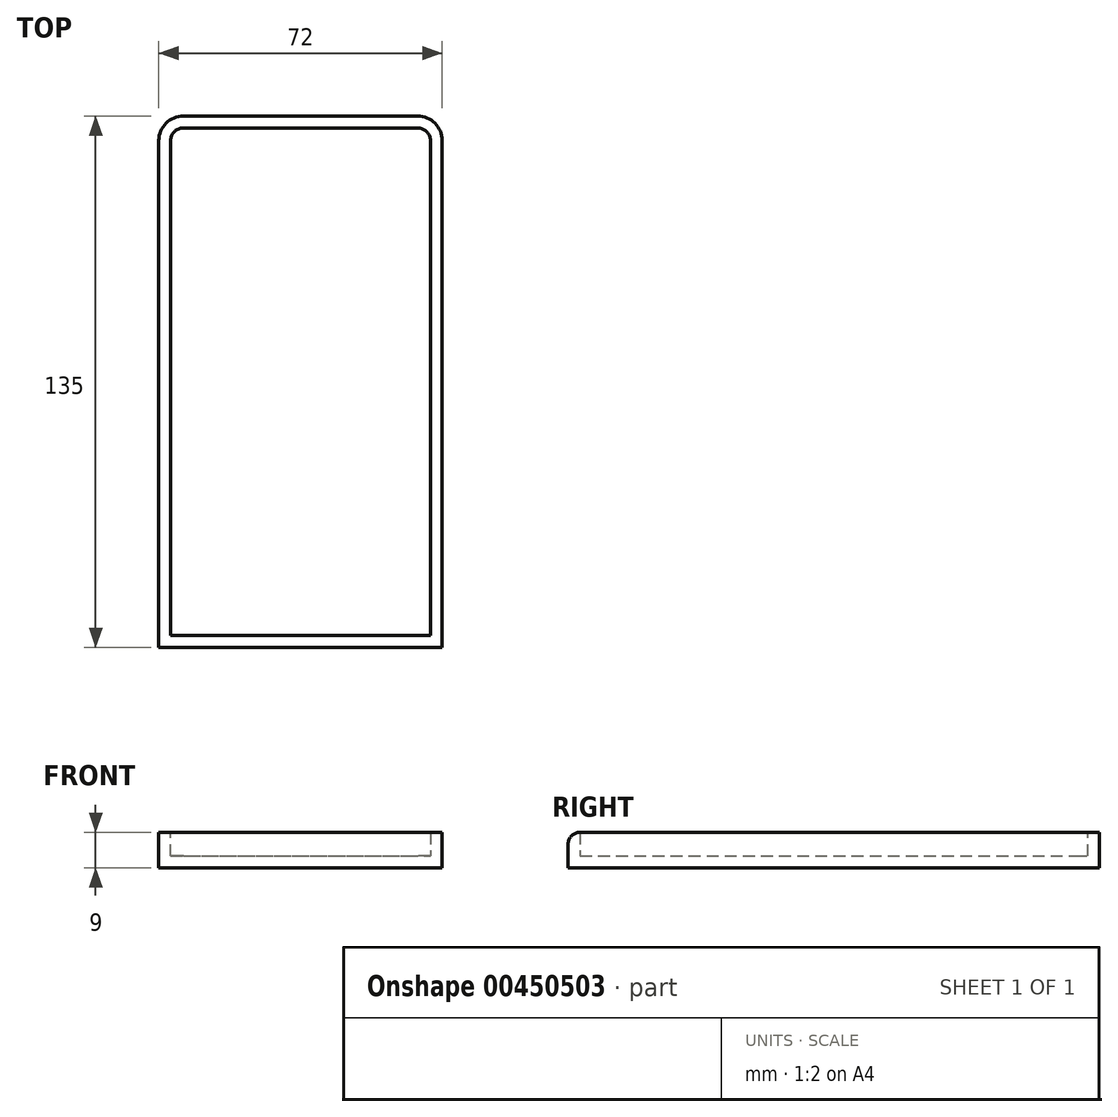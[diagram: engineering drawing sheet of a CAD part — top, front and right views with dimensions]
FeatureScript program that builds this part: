
annotation { "Feature Type Name" : "Feature", "Feature Type Description" : "" }
export const myFeature = defineFeature(function(context is Context, id is Id, definition is map)
    precondition{}
    {
        {
            var Q0;
            Q0=qCreatedBy(makeId("Top.planeOp"),FACE);
            var sketch = newSketch(context, id + "F0", { "sketchPlane" : qUnion([Q0])});
            skLineSegment(sketch, "E0.bottom", {"start": v(-74.36, -53.55) * mm, "end": v(-2.36, -53.55) * mm});
            skLineSegment(sketch, "E0.top", {"start": v(-68.1, 81.45) * mm, "end": v(-8.6, 81.45) * mm});
            skLineSegment(sketch, "E0.left", {"start": v(-74.36, -53.55) * mm, "end": v(-74.36, 75.2) * mm});
            skLineSegment(sketch, "E0.right", {"start": v(-2.36, -53.55) * mm, "end": v(-2.36, 75.2) * mm});
            skPoint(sketch, "E1.visualSharp", {"position": v(-74.36, 81.45) * mm});
            skArc(sketch, "E1.filletArc", {"start": v(-68.1, 81.45) * mm, "mid": v(-72.53, 79.62) * mm, "end": v(-74.36, 75.2) * mm});
            skPoint(sketch, "E2.visualSharp", {"position": v(-2.36, 81.45) * mm});
            skArc(sketch, "E2.filletArc", {"start": v(-2.36, 75.2) * mm, "mid": v(-4.19, 79.62) * mm, "end": v(-8.6, 81.45) * mm});
            skSolve(sketch);
        }
        {
            var Q0;
            Q0=makeQuery(id+"F0.imprint","IMPRINT",FACE,{"disambiguationData":[TD([[makeQuery(id+"F0.imprint","IMPRINT",EDGE,{"derivedFrom":sQuery(id+"F0.wireOp",EDGE,"E0.bottom")}),1.0]])]});
            extrude(context, id + "F1", {"entities" : qUnion([Q0]), "depth" : 9 * mm});
        }
        {
            var Q0;
            Q0=makeQuery(id+"F1.opExtrude","CAP_FACE",FACE,{"disambiguationData":[OSD([sQuery(id+"F0.wireOp",EDGE,"E0.bottom"),sQuery(id+"F0.wireOp",EDGE,"E0.top"),sQuery(id+"F0.wireOp",EDGE,"E0.left"),sQuery(id+"F0.wireOp",EDGE,"E0.right")])],"isStart":false});
            shell(context, id + "F2", {"entities" : qUnion([Q0]), "thickness" : 3 * mm});
        }
        {
            var Q0;
            Q0=makeQuery(id+"F1.opExtrude","CAP_EDGE",EDGE,{"disambiguationData":[OSD([sQuery(id+"F0.wireOp",EDGE,"E0.bottom")])],"isStart":false});
            fillet(context, id + "F3", {"entities" : qUnion([Q0]), "radius" : 3 * mm, "tangentPropagation" : true, "allowEdgeOverflow" : false});
        }
    });
